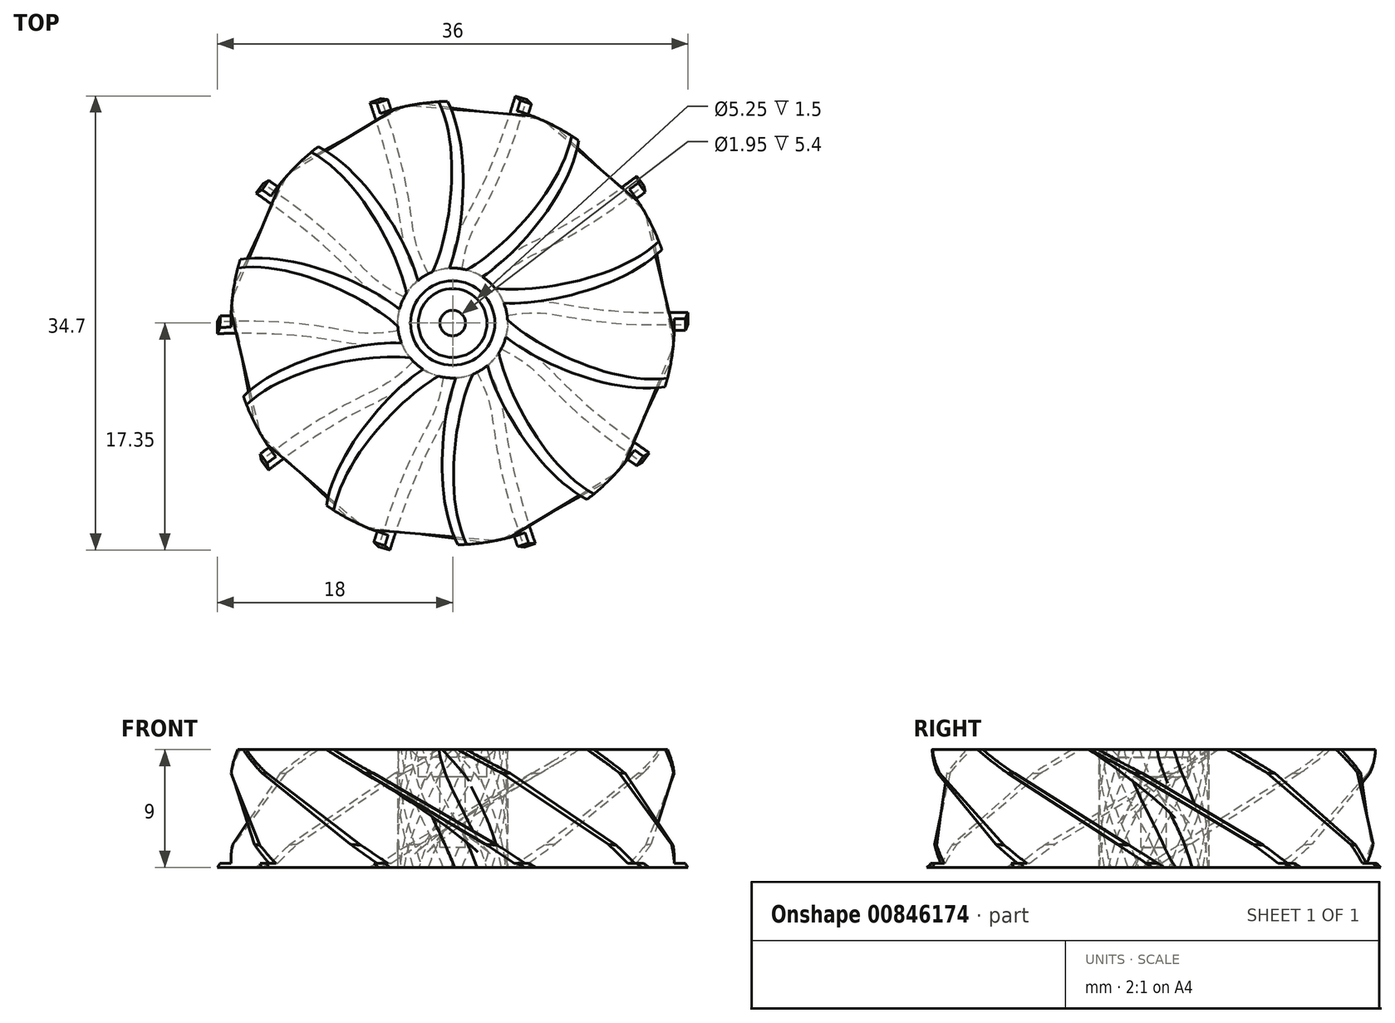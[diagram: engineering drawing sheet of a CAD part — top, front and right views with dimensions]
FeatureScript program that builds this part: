
annotation { "Feature Type Name" : "Feature", "Feature Type Description" : "" }
export const myFeature = defineFeature(function(context is Context, id is Id, definition is map)
    precondition{}
    {
        {
            var Q0;
            Q0=qCreatedBy(makeId("Top.planeOp"),FACE);
            var sketch = newSketch(context, id + "F0", { "sketchPlane" : qUnion([Q0])});
            skCircle(sketch, "E0", {"center": v(0, 0) * mm, "radius": 14 * mm});
            skSolve(sketch);
        }
        {
            var Q0;
            Q0=qSketchRegion(id+"F0",true);
            extrude(context, id + "F1", {"entities" : qUnion([Q0]), "depth" : 30 * mm, "offsetDistance" : 25 * mm});
        }
        {
            var Q0;
            Q0=makeQuery(id+"F1.opExtrude","CAP_FACE",FACE,{"disambiguationData":[OSD([sQuery(id+"F0.wireOp",EDGE,"E0")])],"isStart":false});
            var sketch = newSketch(context, id + "F2", { "sketchPlane" : qUnion([Q0])});
            skLineSegment(sketch, "E1", {"start": v(0, 0) * mm, "end": v(0, 60) * mm, "construction": true});
            skLineSegment(sketch, "E2", {"start": v(-9, 10) * mm, "end": v(-6, 10) * mm});
            skLineSegment(sketch, "E3", {"start": v(-6, 10) * mm, "end": v(0, 10) * mm, "construction": true});
            skLineSegment(sketch, "E4", {"start": v(-5.73, 60) * mm, "end": v(-3.51, 60) * mm});
            skFitSpline(sketch, "E5", {"points": [v(-5.73, 60) * mm, v(-9, 10) * mm], "startDerivative": vector(36.18, -47.87) * mm, "endDerivative": vector(-13.5, 15) * mm});
            skLineSegment(sketch, "E6", {"start": v(0, 0) * mm, "end": v(-9, 10) * mm, "construction": true});
            skLineSegment(sketch, "E7", {"start": v(-5.73, 60) * mm, "end": v(0, 52.42) * mm, "construction": true});
            skPoint(sketch, "E8", {"position": v(-3, 10) * mm});
            skFitSpline(sketch, "E9", {"points": [v(-6, 10) * mm, v(-3.51, 60) * mm], "startDerivative": vector(18, -20) * mm, "endDerivative": vector(-36.94, 47.28) * mm});
            skLineSegment(sketch, "E10", {"start": v(-6, 10) * mm, "end": v(3.4, -0.45) * mm, "construction": true});
            skLineSegment(sketch, "E11", {"start": v(-3.49, -3.14) * mm, "end": v(0, 0) * mm, "construction": true});
            skLineSegment(sketch, "E12", {"start": v(1.66, 1.5) * mm, "end": v(3.4, -0.45) * mm, "construction": true});
            skLineSegment(sketch, "E13", {"start": v(-3.51, 60) * mm, "end": v(3.6, 60) * mm, "construction": true});
            skLineSegment(sketch, "E14", {"start": v(-3.51, 60) * mm, "end": v(-0.35, 55.96) * mm, "construction": true});
            skPoint(sketch, "E15", {"position": v(0, 30) * mm});
            skSolve(sketch);
        }
        {
            var Q0;
            Q0=makeQuery(id+"F0.imprint","IMPRINT",FACE,{"disambiguationData":[TD([[makeQuery(id+"F0.imprint","IMPRINT",EDGE,{"derivedFrom":sQuery(id+"F0.wireOp",EDGE,"E0")}),1.0]])]});
            var sketch = newSketch(context, id + "F3", { "sketchPlane" : qUnion([Q0])});
            skLineSegment(sketch, "E16", {"start": v(0, 0) * mm, "end": v(0.51, 1.4) * mm});
            skLineSegment(sketch, "E17", {"start": v(0.51, 1.4) * mm, "end": v(0, 0) * mm});
            skLineSegment(sketch, "E18", {"start": v(0, 0) * mm, "end": v(-0.51, -1.4) * mm});
            skCircle(sketch, "E19", {"center": v(0, 0) * mm, "radius": 60 * mm, "construction": true});
            skFitSpline(sketch, "E20", {"points": [v(-0.51, -1.4) * mm, v(-50.07, 33.06) * mm], "startDerivative": vector(-91.96, 33.47) * mm, "endDerivative": vector(-100.37, 69.94) * mm});
            skFitSpline(sketch, "E21.0", {"points": [v(0.51, 1.4) * mm, v(-3.28, 2.8) * mm, v(-9.44, 5.2) * mm, v(-14.4, 7.6) * mm, v(-17.27, 9.35) * mm, v(-19.04, 10.62) * mm, v(-20.6, 11.93) * mm, v(-22.12, 13.37) * mm, v(-23.74, 15.02) * mm, v(-25.58, 16.91) * mm, v(-27.77, 19.09) * mm, v(-31.3, 22.4) * mm, v(-37.17, 27.4) * mm, v(-44.13, 32.58) * mm, v(-48.36, 35.52) * mm]});
            skLineSegment(sketch, "E22", {"start": v(0.51, 1.4) * mm, "end": v(0.51, 1.4) * mm});
            skLineSegment(sketch, "E23", {"start": v(-50.07, 33.06) * mm, "end": v(-48.36, 35.52) * mm});
            skSolve(sketch);
        }
        {
            var Q1;
            {var subQ0=sQuery(id+"F2.wireOp",EDGE,"E4");Q1=makeQuery(id+"F2.imprint","IMPRINT",FACE,{"disambiguationData":[TD([[makeQuery(id+"F2.imprint","IMPRINT",EDGE,{"derivedFrom":subQ0}),-1.0]])]});}
            var Q2;
            {var subQ0=sQuery(id+"F3.wireOp",EDGE,"E23");Q2=makeQuery(id+"F3.imprint","IMPRINT",FACE,{"disambiguationData":[TD([[makeQuery(id+"F3.imprint","IMPRINT",EDGE,{"derivedFrom":subQ0}),-1.0]])]});}
            loft(context, id + "F4", {"operationType" : NewBodyOperationType.ADD, "sheetProfilesArray" : [{ "sheetProfileEntities" : qUnion([Q1]) }, { "sheetProfileEntities" : qUnion([Q2]) }]});
        }
        {
            var Q0;
            Q0=qCreatedBy(makeId("Right.planeOp"),FACE);
            var sketch = newSketch(context, id + "F5", { "sketchPlane" : qUnion([Q0])});
            skLineSegment(sketch, "E24", {"start": v(0, -18.68) * mm, "end": v(0, 32.68) * mm, "construction": true});
            skSolve(sketch);
        }
        {
            var Q0;
            Q0=makeQuery(id+"F1.opExtrude","SWEPT_BODY",BODY,{"disambiguationData":[OSD([sQuery(id+"F0.wireOp",EDGE,"E0")])]});
            var Q1;
            Q1=sQuery(id+"F5.wireOp",EDGE,"E24");
            circularPattern(context, id + "F6", {"entities" : qUnion([Q0]), "axis" : qUnion([Q1]), "angle" : 360 * degree, "instanceCount" : 10, "equalSpace" : true});
        }
        {
            var Q0;
            Q0=makeQuery(id+"F1.opExtrude","SWEPT_BODY",BODY,{"disambiguationData":[OSD([sQuery(id+"F0.wireOp",EDGE,"E0")])]});
            var Q1;
            Q1=makeQuery(id+"F6.opPattern","COPY",BODY,{"derivedFrom":makeQuery(id+"F1.opExtrude","SWEPT_BODY",BODY,{"disambiguationData":[OSD([sQuery(id+"F0.wireOp",EDGE,"E0")])]}),"instanceName":"1"});
            var Q2;
            Q2=makeQuery(id+"F6.opPattern","COPY",BODY,{"derivedFrom":makeQuery(id+"F1.opExtrude","SWEPT_BODY",BODY,{"disambiguationData":[OSD([sQuery(id+"F0.wireOp",EDGE,"E0")])]}),"instanceName":"2"});
            var Q3;
            Q3=makeQuery(id+"F6.opPattern","COPY",BODY,{"derivedFrom":makeQuery(id+"F1.opExtrude","SWEPT_BODY",BODY,{"disambiguationData":[OSD([sQuery(id+"F0.wireOp",EDGE,"E0")])]}),"instanceName":"3"});
            var Q4;
            Q4=makeQuery(id+"F6.opPattern","COPY",BODY,{"derivedFrom":makeQuery(id+"F1.opExtrude","SWEPT_BODY",BODY,{"disambiguationData":[OSD([sQuery(id+"F0.wireOp",EDGE,"E0")])]}),"instanceName":"4"});
            var Q5;
            Q5=makeQuery(id+"F6.opPattern","COPY",BODY,{"derivedFrom":makeQuery(id+"F1.opExtrude","SWEPT_BODY",BODY,{"disambiguationData":[OSD([sQuery(id+"F0.wireOp",EDGE,"E0")])]}),"instanceName":"5"});
            var Q6;
            Q6=makeQuery(id+"F6.opPattern","COPY",BODY,{"derivedFrom":makeQuery(id+"F1.opExtrude","SWEPT_BODY",BODY,{"disambiguationData":[OSD([sQuery(id+"F0.wireOp",EDGE,"E0")])]}),"instanceName":"6"});
            var Q7;
            Q7=makeQuery(id+"F6.opPattern","COPY",BODY,{"derivedFrom":makeQuery(id+"F1.opExtrude","SWEPT_BODY",BODY,{"disambiguationData":[OSD([sQuery(id+"F0.wireOp",EDGE,"E0")])]}),"instanceName":"7"});
            var Q8;
            Q8=makeQuery(id+"F6.opPattern","COPY",BODY,{"derivedFrom":makeQuery(id+"F1.opExtrude","SWEPT_BODY",BODY,{"disambiguationData":[OSD([sQuery(id+"F0.wireOp",EDGE,"E0")])]}),"instanceName":"8"});
            var Q9;
            Q9=makeQuery(id+"F6.opPattern","COPY",BODY,{"derivedFrom":makeQuery(id+"F1.opExtrude","SWEPT_BODY",BODY,{"disambiguationData":[OSD([sQuery(id+"F0.wireOp",EDGE,"E0")])]}),"instanceName":"9"});
            var Q10;
            Q10=makeQuery(id+"F6.opPattern","COPY",BODY,{"derivedFrom":makeQuery(id+"F1.opExtrude","SWEPT_BODY",BODY,{"disambiguationData":[OSD([sQuery(id+"F0.wireOp",EDGE,"E0")])]}),"instanceName":"10"});
            var Q11;
            Q11=makeQuery(id+"F6.opPattern","COPY",BODY,{"derivedFrom":makeQuery(id+"F1.opExtrude","SWEPT_BODY",BODY,{"disambiguationData":[OSD([sQuery(id+"F0.wireOp",EDGE,"E0")])]}),"instanceName":"11"});
            var Q12;
            Q12=makeQuery(id+"F6.opPattern","COPY",BODY,{"derivedFrom":makeQuery(id+"F1.opExtrude","SWEPT_BODY",BODY,{"disambiguationData":[OSD([sQuery(id+"F0.wireOp",EDGE,"E0")])]}),"instanceName":"12"});
            var Q13;
            Q13=makeQuery(id+"F6.opPattern","COPY",BODY,{"derivedFrom":makeQuery(id+"F1.opExtrude","SWEPT_BODY",BODY,{"disambiguationData":[OSD([sQuery(id+"F0.wireOp",EDGE,"E0")])]}),"instanceName":"13"});
            var Q14;
            Q14=makeQuery(id+"F6.opPattern","COPY",BODY,{"derivedFrom":makeQuery(id+"F1.opExtrude","SWEPT_BODY",BODY,{"disambiguationData":[OSD([sQuery(id+"F0.wireOp",EDGE,"E0")])]}),"instanceName":"14"});
            var Q15;
            Q15=makeQuery(id+"F6.opPattern","COPY",BODY,{"derivedFrom":makeQuery(id+"F1.opExtrude","SWEPT_BODY",BODY,{"disambiguationData":[OSD([sQuery(id+"F0.wireOp",EDGE,"E0")])]}),"instanceName":"15"});
            booleanBodies(context, id + "F7", {"operationType" : BooleanOperationType.UNION, "tools" : qUnion([Q0, Q1, Q2, Q3, Q4, Q5, Q6, Q7, Q8, Q9, Q10, Q11, Q12, Q13, Q14, Q15])});
        }
        {
            var Q0;
            {var subQ0=sQuery(id+"F2.wireOp",EDGE,"E4");var subQ2=sQuery(id+"F0.wireOp",EDGE,"E0");var subQ7=makeQuery(id+"F4.boolean.opBoolean","MERGE",FACE,{"derivedFrom":[makeQuery(id+"F1.opExtrude","CAP_FACE",FACE,{"disambiguationData":[OSD([subQ2])],"isStart":false}),makeQuery(id+"F4.opLoft","CAP_FACE",FACE,{"disambiguationData":[OSD([makeQuery(id+"F2.imprint","IMPRINT",FACE,{"disambiguationData":[TD([[makeQuery(id+"F2.imprint","IMPRINT",EDGE,{"derivedFrom":subQ0}),-1.0]])]})])],"isStart":true})]});Q0=makeQuery(id+"F7.opBoolean","MERGE",FACE,{"derivedFrom":[subQ7,makeQuery(id+"F6.opPattern","COPY",FACE,{"derivedFrom":subQ7,"instanceName":"1"}),makeQuery(id+"F6.opPattern","COPY",FACE,{"derivedFrom":subQ7,"instanceName":"2"}),makeQuery(id+"F6.opPattern","COPY",FACE,{"derivedFrom":subQ7,"instanceName":"3"}),makeQuery(id+"F6.opPattern","COPY",FACE,{"derivedFrom":subQ7,"instanceName":"4"}),makeQuery(id+"F6.opPattern","COPY",FACE,{"derivedFrom":subQ7,"instanceName":"5"}),makeQuery(id+"F6.opPattern","COPY",FACE,{"derivedFrom":subQ7,"instanceName":"6"}),makeQuery(id+"F6.opPattern","COPY",FACE,{"derivedFrom":subQ7,"instanceName":"7"}),makeQuery(id+"F6.opPattern","COPY",FACE,{"derivedFrom":subQ7,"instanceName":"8"}),makeQuery(id+"F6.opPattern","COPY",FACE,{"derivedFrom":subQ7,"instanceName":"9"}),makeQuery(id+"F6.opPattern","COPY",FACE,{"derivedFrom":subQ7,"instanceName":"10"}),makeQuery(id+"F6.opPattern","COPY",FACE,{"derivedFrom":subQ7,"instanceName":"11"}),makeQuery(id+"F6.opPattern","COPY",FACE,{"derivedFrom":subQ7,"instanceName":"12"}),makeQuery(id+"F6.opPattern","COPY",FACE,{"derivedFrom":subQ7,"instanceName":"13"}),makeQuery(id+"F6.opPattern","COPY",FACE,{"derivedFrom":subQ7,"instanceName":"14"}),makeQuery(id+"F6.opPattern","COPY",FACE,{"derivedFrom":subQ7,"instanceName":"15"})]});}
            var sketch = newSketch(context, id + "F8", { "sketchPlane" : qUnion([Q0])});
            skCircle(sketch, "E25", {"center": v(0, 0) * mm, "radius": 3.25 * mm});
            skSolve(sketch);
        }
        {
            var Q0;
            Q0=qSketchRegion(id+"F8",true);
            extrude(context, id + "F9", {"entities" : qUnion([Q0]), "operationType" : NewBodyOperationType.ADD, "depth" : 1 * mm, "offsetDistance" : 25 * mm});
        }
        {
            var Q0;
            Q0=makeQuery(id+"F9.opExtrude","CAP_FACE",FACE,{"disambiguationData":[OSD([sQuery(id+"F8.wireOp",EDGE,"E25")])],"isStart":false});
            var sketch = newSketch(context, id + "F10", { "sketchPlane" : qUnion([Q0])});
            skCircle(sketch, "E26", {"center": v(0, 0) * mm, "radius": 56.5 * mm});
            skCircle(sketch, "E27.0", {"center": v(0, 0) * mm, "radius": 61.5 * mm});
            skSolve(sketch);
        }
        {
            var Q0;
            Q0=qSketchRegion(id+"F10",true);
            extrude(context, id + "F11", {"entities" : qUnion([Q0]), "operationType" : NewBodyOperationType.REMOVE, "oppositeDirection" : true, "depth" : 30 * mm, "offsetDistance" : 25 * mm});
        }
        {
            var Q0;
            Q0=qSketchRegion(id+"F8",true);
            extrude(context, id + "F12", {"entities" : qUnion([Q0]), "operationType" : NewBodyOperationType.REMOVE, "oppositeDirection" : true, "depth" : 25 * mm, "offsetDistance" : 25 * mm, "hasSecondDirection" : true, "secondDirectionOppositeDirection" : false, "secondDirectionDepth" : 25 * mm});
        }
        {
            var Q0;
            Q0=makeQuery(id+"F10.imprint","IMPRINT",FACE,{"disambiguationData":[TD([[makeQuery(id+"F10.imprint","IMPRINT",EDGE,{"derivedFrom":sQuery(id+"F10.wireOp",EDGE,"E26")}),1.0]])]});
            var sketch = newSketch(context, id + "F13", { "sketchPlane" : qUnion([Q0])});
            skCircle(sketch, "E28", {"center": v(0, 0) * mm, "radius": 8.75 * mm});
            skSolve(sketch);
        }
        {
            var Q0;
            Q0=qSketchRegion(id+"F13",true);
            extrude(context, id + "F14", {"entities" : qUnion([Q0]), "operationType" : NewBodyOperationType.REMOVE, "oppositeDirection" : true, "depth" : 8 * mm, "offsetDistance" : 25 * mm});
        }
        {
            var Q0;
            {var subQ0=sQuery(id+"F2.wireOp",EDGE,"E4");var subQ2=sQuery(id+"F0.wireOp",EDGE,"E0");var subQ7=makeQuery(id+"F4.boolean.opBoolean","MERGE",FACE,{"derivedFrom":[makeQuery(id+"F1.opExtrude","CAP_FACE",FACE,{"disambiguationData":[OSD([subQ2])],"isStart":false}),makeQuery(id+"F4.opLoft","CAP_FACE",FACE,{"disambiguationData":[OSD([makeQuery(id+"F2.imprint","IMPRINT",FACE,{"disambiguationData":[TD([[makeQuery(id+"F2.imprint","IMPRINT",EDGE,{"derivedFrom":subQ0}),-1.0]])]})])],"isStart":true})]});Q0=makeQuery(id+"F14.boolean.opBoolean","INTERSECT",EDGE,{"derivedFrom":[makeQuery(id+"F7.opBoolean","MERGE",FACE,{"derivedFrom":[subQ7,makeQuery(id+"F6.opPattern","COPY",FACE,{"derivedFrom":subQ7,"instanceName":"1"}),makeQuery(id+"F6.opPattern","COPY",FACE,{"derivedFrom":subQ7,"instanceName":"2"}),makeQuery(id+"F6.opPattern","COPY",FACE,{"derivedFrom":subQ7,"instanceName":"3"}),makeQuery(id+"F6.opPattern","COPY",FACE,{"derivedFrom":subQ7,"instanceName":"4"}),makeQuery(id+"F6.opPattern","COPY",FACE,{"derivedFrom":subQ7,"instanceName":"5"}),makeQuery(id+"F6.opPattern","COPY",FACE,{"derivedFrom":subQ7,"instanceName":"6"}),makeQuery(id+"F6.opPattern","COPY",FACE,{"derivedFrom":subQ7,"instanceName":"7"}),makeQuery(id+"F6.opPattern","COPY",FACE,{"derivedFrom":subQ7,"instanceName":"8"}),makeQuery(id+"F6.opPattern","COPY",FACE,{"derivedFrom":subQ7,"instanceName":"9"})]}),makeQuery(id+"F14.opExtrude","SWEPT_FACE",FACE,{"disambiguationData":[OSD([sQuery(id+"F13.wireOp",EDGE,"E28")])]})]});}
            chamfer(context, id + "F15", {"entities" : qUnion([Q0]), "width" : 2 * mm, "tangentPropagation" : true});
        }
        {
            var Q0;
            Q0=makeQuery(id+"F1.opExtrude","SWEPT_BODY",BODY,{"disambiguationData":[OSD([sQuery(id+"F0.wireOp",EDGE,"E0")])]});
            var Q1;
            Q1=sQuery(id+"F0.wireOp",VERTEX,"E0.center");
            transform(context, id + "F16", {"entities" : qUnion([Q0]), "transformType" : TransformType.SCALE_UNIFORMLY, "scale" : 0.3, "scalePoint" : qUnion([Q1]), "makeCopy" : false});
        }
    });
